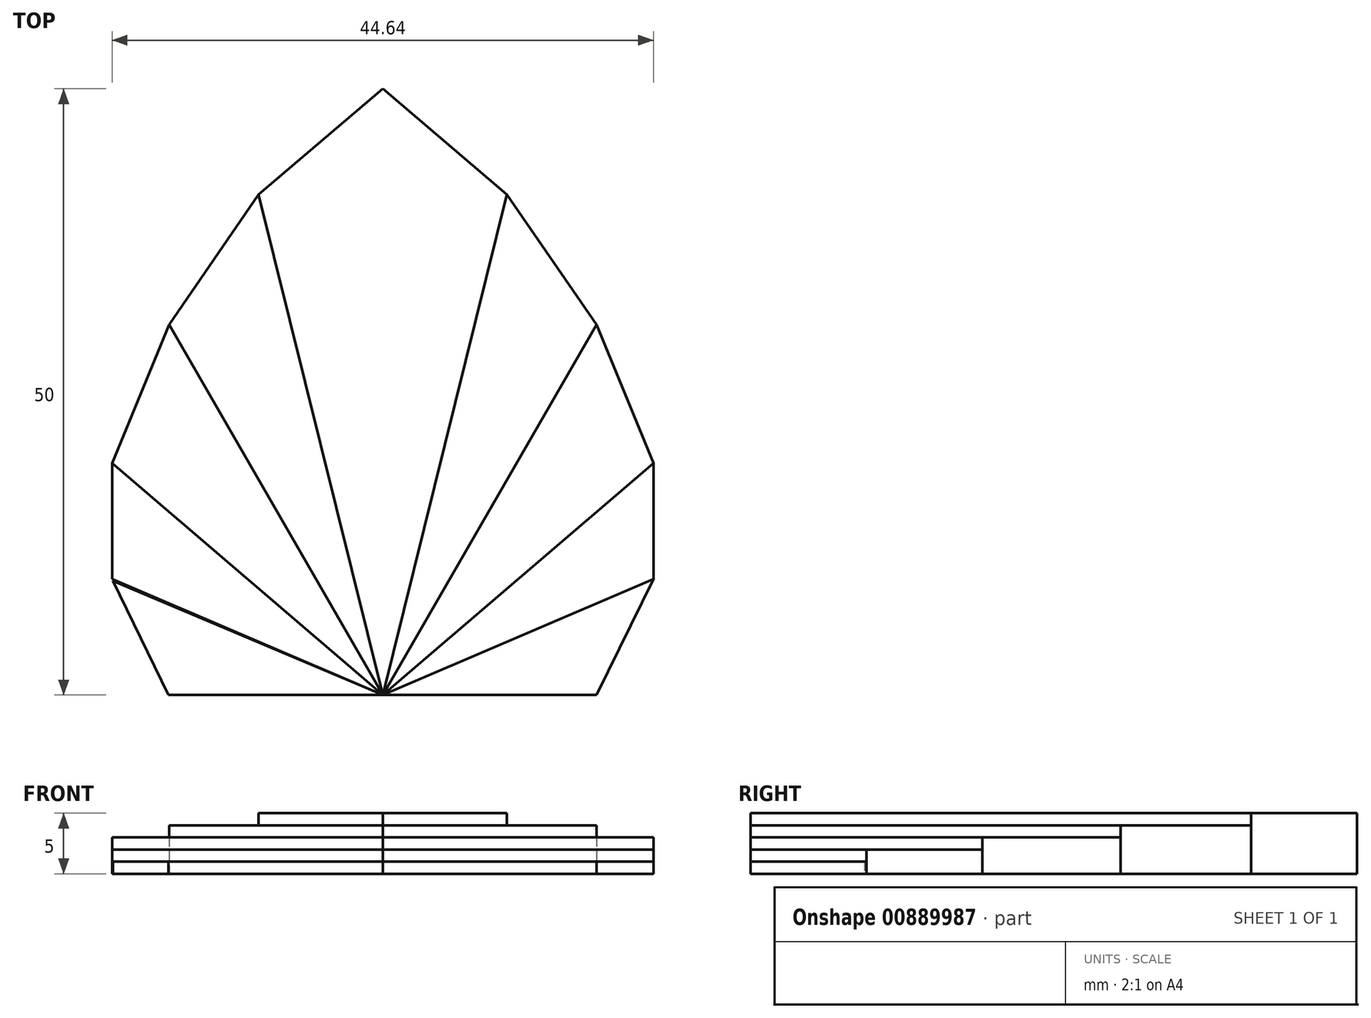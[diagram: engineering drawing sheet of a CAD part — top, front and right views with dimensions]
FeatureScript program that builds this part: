
annotation { "Feature Type Name" : "Feature", "Feature Type Description" : "" }
export const myFeature = defineFeature(function(context is Context, id is Id, definition is map)
    precondition{}
    {
        {
            var Q0;
            Q0=qCreatedBy(makeId("Top.planeOp"),FACE);
            var sketch = newSketch(context, id + "F0", { "sketchPlane" : qUnion([Q0])});
            skLineSegment(sketch, "E0", {"start": v(0, 0) * mm, "end": v(10.23, 41.28) * mm});
            skLineSegment(sketch, "E1", {"start": v(10.23, 41.28) * mm, "end": v(0, 50) * mm});
            skLineSegment(sketch, "E2", {"start": v(0, 50) * mm, "end": v(0, 0) * mm});
            skLineSegment(sketch, "E3", {"start": v(0, 0) * mm, "end": v(17.62, 30.54) * mm});
            skLineSegment(sketch, "E4", {"start": v(17.62, 30.54) * mm, "end": v(10.23, 41.28) * mm});
            skLineSegment(sketch, "E5", {"start": v(0, 0) * mm, "end": v(22.32, 19.13) * mm});
            skLineSegment(sketch, "E6", {"start": v(22.32, 19.13) * mm, "end": v(17.62, 30.54) * mm});
            skLineSegment(sketch, "E7", {"start": v(0, 0) * mm, "end": v(22.32, 9.56) * mm});
            skPoint(sketch, "E7.endSnap0", {"position": v(11.16, 9.56) * mm});
            skLineSegment(sketch, "E8", {"start": v(22.32, 9.56) * mm, "end": v(22.32, 19.13) * mm});
            skLineSegment(sketch, "E9", {"start": v(0, 0) * mm, "end": v(17.62, 0) * mm});
            skLineSegment(sketch, "E10", {"start": v(17.62, 0) * mm, "end": v(22.32, 9.56) * mm});
            skLineSegment(sketch, "E11.MirrorCS", {"start": v(-10.23, 41.28) * mm, "end": v(0, 50) * mm});
            skLineSegment(sketch, "E12.MirrorCS", {"start": v(0, 0) * mm, "end": v(-10.23, 41.28) * mm});
            skLineSegment(sketch, "E13.MirrorCS", {"start": v(-17.62, 30.54) * mm, "end": v(-10.23, 41.28) * mm});
            skLineSegment(sketch, "E14.MirrorCS", {"start": v(0, 0) * mm, "end": v(-17.62, 30.54) * mm});
            skLineSegment(sketch, "E15.MirrorCS", {"start": v(-22.32, 19.13) * mm, "end": v(-17.62, 30.54) * mm});
            skLineSegment(sketch, "E16.MirrorCS", {"start": v(0, 0) * mm, "end": v(-22.32, 19.13) * mm});
            skLineSegment(sketch, "E17.MirrorCS", {"start": v(-22.32, 9.56) * mm, "end": v(-22.32, 19.13) * mm});
            skLineSegment(sketch, "E18.MirrorCS", {"start": v(-17.62, 0) * mm, "end": v(-22.32, 9.56) * mm});
            skLineSegment(sketch, "E19.MirrorCS", {"start": v(0, 0) * mm, "end": v(-22.32, 9.56) * mm});
            skLineSegment(sketch, "E20.MirrorCS", {"start": v(0, 0) * mm, "end": v(-17.62, 0) * mm});
            skSolve(sketch);
        }
        {
            var Q0;
            Q0=qCreatedBy(makeId("Top.planeOp"),FACE);
            var sketch = newSketch(context, id + "F1", { "sketchPlane" : qUnion([Q0])});
            skLineSegment(sketch, "E21", {"start": v(0, 0) * mm, "end": v(-22.26, 9.41) * mm});
            skLineSegment(sketch, "E22", {"start": v(-22.26, 9.41) * mm, "end": v(-17.68, 0) * mm});
            skLineSegment(sketch, "E23", {"start": v(-17.68, 0) * mm, "end": v(0, 0) * mm});
            skSolve(sketch);
        }
        {
            var Q0;
            Q0 = qSketchRegion(id + "F1", true);
            extrude(context, id + "F2", {"entities" : qUnion([Q0]), "depth" : 1 * mm, "offsetDistance" : 25.4 * mm});
        }
        {
            var Q0;
            Q0=qCreatedBy(makeId("Top.planeOp"),FACE);
            var sketch = newSketch(context, id + "F3", { "sketchPlane" : qUnion([Q0])});
            skSolve(sketch);
        }
        {
            var Q0;
            Q0 = qSketchRegion(id + "F3", true);
            var Q1;
            Q1=makeQuery(id+"F0.imprint","IMPRINT",FACE,{"disambiguationData":[TD([[makeQuery(id+"F0.imprint","IMPRINT",EDGE,{"derivedFrom":sQuery(id+"F0.wireOp",EDGE,"E16.MirrorCS")}),1.0]])]});
            extrude(context, id + "F4", {"entities" : qUnion([Q0, Q1]), "depth" : 2 * mm, "offsetDistance" : 25.4 * mm});
        }
        {
            var Q0;
            Q0=qCreatedBy(makeId("Top.planeOp"),FACE);
            var sketch = newSketch(context, id + "F5", { "sketchPlane" : qUnion([Q0])});
            skSolve(sketch);
        }
        {
            var Q0;
            Q0=makeQuery(id+"F0.imprint","IMPRINT",FACE,{"disambiguationData":[TD([[makeQuery(id+"F0.imprint","IMPRINT",EDGE,{"derivedFrom":sQuery(id+"F0.wireOp",EDGE,"E14.MirrorCS")}),1.0]])]});
            var Q1;
            Q1 = qSketchRegion(id + "F5", true);
            extrude(context, id + "F6", {"entities" : qUnion([Q0, Q1]), "operationType" : NewBodyOperationType.ADD, "depth" : 3 * mm, "offsetDistance" : 25.4 * mm});
        }
        {
            var Q0;
            Q0=makeQuery(id+"F0.imprint","IMPRINT",FACE,{"disambiguationData":[TD([[makeQuery(id+"F0.imprint","IMPRINT",EDGE,{"derivedFrom":sQuery(id+"F0.wireOp",EDGE,"E12.MirrorCS")}),1.0]])]});
            var sketch = newSketch(context, id + "F7", { "sketchPlane" : qUnion([Q0])});
            skSolve(sketch);
        }
        {
            var Q0;
            Q0=makeQuery(id+"F7.imprint","IMPRINT",FACE,{"disambiguationData":[TD([[makeQuery(id+"F7.imprint","IMPRINT",EDGE,{"derivedFrom":makeQuery(id+"F0.imprint","IMPRINT",EDGE,{"derivedFrom":sQuery(id+"F0.wireOp",EDGE,"E12.MirrorCS")})}),1.0]])]});
            extrude(context, id + "F8", {"entities" : qUnion([Q0]), "operationType" : NewBodyOperationType.ADD, "depth" : 4 * mm, "offsetDistance" : 25.4 * mm});
        }
        {
            var Q0;
            Q0=makeQuery(id+"F0.imprint","IMPRINT",FACE,{"disambiguationData":[TD([[makeQuery(id+"F0.imprint","IMPRINT",EDGE,{"derivedFrom":sQuery(id+"F0.wireOp",EDGE,"E2")}),-1.0]])]});
            extrude(context, id + "F9", {"entities" : qUnion([Q0]), "operationType" : NewBodyOperationType.ADD, "depth" : 5 * mm, "offsetDistance" : 25.4 * mm});
        }
        {
            var Q0;
            Q0=makeQuery(id+"F0.imprint","IMPRINT",FACE,{"disambiguationData":[TD([[makeQuery(id+"F0.imprint","IMPRINT",EDGE,{"derivedFrom":sQuery(id+"F0.wireOp",EDGE,"E0")}),1.0]])]});
            extrude(context, id + "F10", {"entities" : qUnion([Q0]), "operationType" : NewBodyOperationType.ADD, "depth" : 5 * mm, "offsetDistance" : 25.4 * mm});
        }
        {
            var Q0;
            Q0=makeQuery(id+"F0.imprint","IMPRINT",FACE,{"disambiguationData":[TD([[makeQuery(id+"F0.imprint","IMPRINT",EDGE,{"derivedFrom":sQuery(id+"F0.wireOp",EDGE,"E0")}),-1.0]])]});
            extrude(context, id + "F11", {"entities" : qUnion([Q0]), "operationType" : NewBodyOperationType.ADD, "depth" : 4 * mm, "offsetDistance" : 25.4 * mm});
        }
        {
            var Q0;
            Q0=makeQuery(id+"F0.imprint","IMPRINT",FACE,{"disambiguationData":[TD([[makeQuery(id+"F0.imprint","IMPRINT",EDGE,{"derivedFrom":sQuery(id+"F0.wireOp",EDGE,"E3")}),-1.0]])]});
            extrude(context, id + "F12", {"entities" : qUnion([Q0]), "operationType" : NewBodyOperationType.ADD, "depth" : 3 * mm, "offsetDistance" : 25.4 * mm});
        }
        {
            var Q0;
            Q0=makeQuery(id+"F0.imprint","IMPRINT",FACE,{"disambiguationData":[TD([[makeQuery(id+"F0.imprint","IMPRINT",EDGE,{"derivedFrom":sQuery(id+"F0.wireOp",EDGE,"E5")}),-1.0]])]});
            extrude(context, id + "F13", {"entities" : qUnion([Q0]), "operationType" : NewBodyOperationType.ADD, "depth" : 2 * mm, "offsetDistance" : 25.4 * mm});
        }
        {
            var Q0;
            Q0=makeQuery(id+"F0.imprint","IMPRINT",FACE,{"disambiguationData":[TD([[makeQuery(id+"F0.imprint","IMPRINT",EDGE,{"derivedFrom":sQuery(id+"F0.wireOp",EDGE,"E7")}),-1.0]])]});
            extrude(context, id + "F14", {"entities" : qUnion([Q0]), "operationType" : NewBodyOperationType.ADD, "depth" : 1 * mm, "offsetDistance" : 25.4 * mm});
        }
    });
